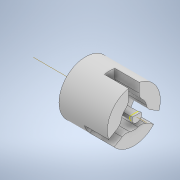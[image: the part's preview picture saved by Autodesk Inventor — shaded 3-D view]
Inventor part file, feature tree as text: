
AUTODESK INVENTOR PART (.ipt)
format: ipt  version: 2022.6 (Build 266554000, 554)  size: 221,696 bytes
history: native  units: mm
features: sketch x9, extrude x6, projected_geometry x4, fillet x1, plane x1, loft x1, other x1
ambient origin geometry x8: Origin, YZ Plane, XZ Plane, XY Plane, X Axis, Y Axis, Z Axis, Center Point
bodies: Solid1 (feature_tree)
feature tree (23):
  extrude  "Extrusion1"  Depth=0.5mm
  extrude  "Extrusion2"  Depth=17.5mm
  extrude  "Extrusion3"  Depth=8.5mm
  extrude  "Extrusion4"  Depth=4.0mm
  fillet  "Fillet1"  Radius=30.0mm
  extrude  "Extrusion5"  Depth=13.3mm
  sketch  "Sketch6"  dims[d20=5.5mm d21=0.0mm d22=10.0mm]
  plane  "Work Plane1"
  sketch  "Sketch7"  dims[d23=3.0mm d24=5.0mm]
  sketch  "Sketch8"  dims[d25=20.0mm d26=0.0mm]
  loft  "Loft1"
  extrude  "Extrusion6"  Depth=5.0mm
  sketch  "Sketch1"  dims[d1=2.8mm d2=0.5mm]
  sketch  "Sketch2"  dims[d3=8.0mm d4=0.0mm d5=17.5mm]
  sketch  "Sketch3"  dims[d6=8.0mm d7=0.0mm d8=8.5mm]
  projected_geometry  "Projected Loop1"
  sketch  "Sketch4"  dims[d9=3.5mm d10=4.0mm d12=30.0mm d14=360.0deg]
  sketch  "Sketch5"  dims[d16=8.0mm d17=0.0mm d19=13.3mm]
  projected_geometry  "Projected Loop2"
  projected_geometry  "Projected Loop3"
  projected_geometry  "Projected Loop4"
  other  "Edges1"
  sketch  "Sketch9"  dims[d27=1.0mm d28=3.2mm d30=0.5mm d31=0.7mm d32=0.0mm d33=90.0deg d34=0.0mm d35=90.0deg d36=6.3mm d37=0.4mm d38=0.0mm d29=0.5mm]
